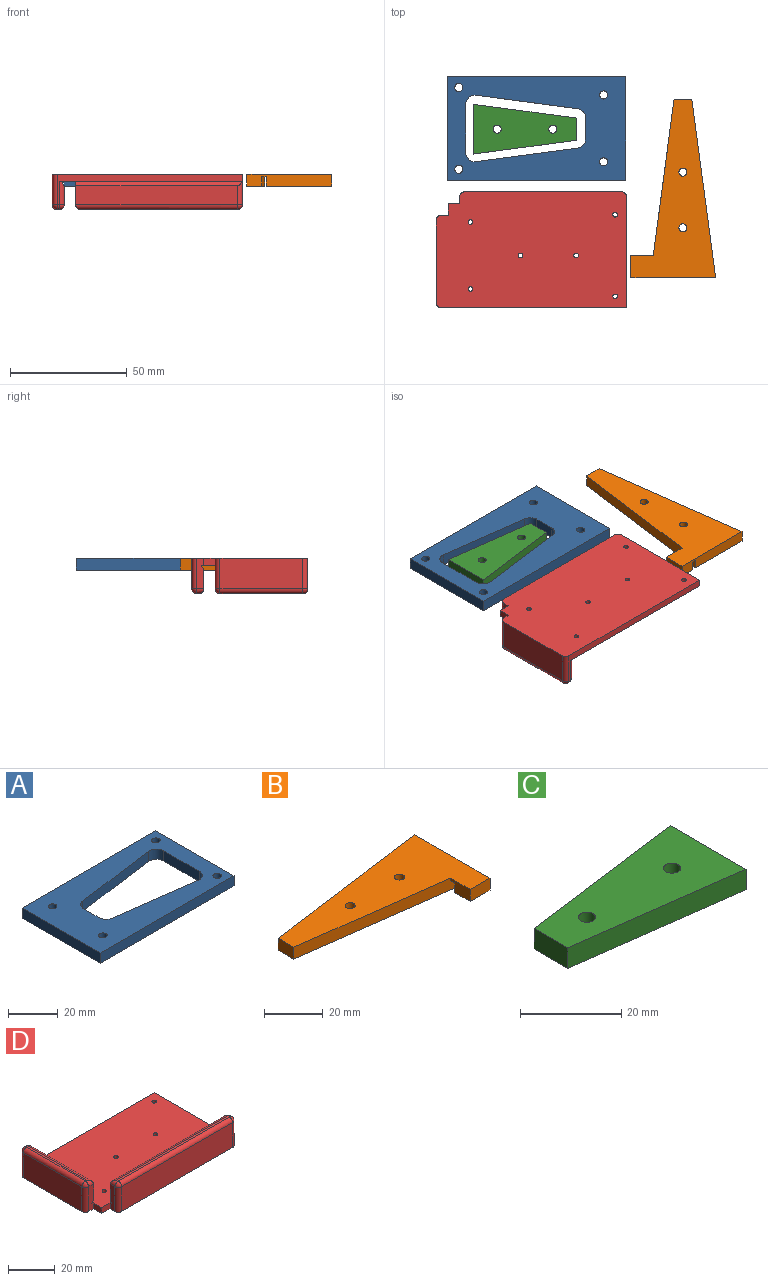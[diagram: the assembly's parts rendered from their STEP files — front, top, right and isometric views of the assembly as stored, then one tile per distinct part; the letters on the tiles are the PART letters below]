
ASSEMBLY  parts=4 mates=6
PART A: 22 faces, bbox 76.2x44.5x5 mm
  f0: plane 43.28x5.77mm, normal (0.13,0.99,0), area 218.3mm2, adj f8,f9,f18,f21
  f1: plane 8.89x5mm, normal (1,0,0), area 44.5mm2, adj f8,f9,f18,f19
  f2: plane 43.28x5.77mm, normal (0.13,-0.99,0), area 218.3mm2, adj f8,f9,f19,f20
  f3: plane 44.45x5mm, normal (-1,0,0), area 222.2mm2, adj f4,f6,f8,f9
  f4: plane 76.2x5mm, normal (0,-1,0), area 381mm2, adj f3,f5,f8,f9
  f5: plane 44.45x5mm, normal (1,0,0), area 222.2mm2, adj f4,f6,f8,f9
  f6: plane 76.2x5mm, normal (0,1,0), area 381mm2, adj f3,f5,f8,f9
  f7: plane 20.43x5mm, normal (-1,0,0), area 102.2mm2, adj f8,f9,f20,f21
  f8: plane 76.2x44.45mm, normal (0,0,-1), area 2075.8mm2, adj f0,f1,f2,f3,f4,f5,f6,f7
  f9: plane 76.2x44.45mm, normal (0,0,1), area 2198.3mm2, adj f0,f1,f2,f3,f4,f5,f6,f7
  f10: cylinder r=1.73mm len=3.45mm, axis (0,0,-1), area 31.3mm2, adj f9,f11
  f11: cone r=1.73mm half-angle=41deg, axis (0,0,-1), area 46.7mm2, adj f8,f10
  f12: cylinder r=1.73mm len=3.45mm, axis (0,0,-1), area 31.3mm2, adj f9,f13
  f13: cone r=1.73mm half-angle=41deg, axis (0,0,-1), area 46.7mm2, adj f8,f12
  f14: cylinder r=1.73mm len=3.45mm, axis (0,0,-1), area 31.3mm2, adj f9,f15
  f15: cone r=1.73mm half-angle=41deg, axis (0,0,-1), area 46.7mm2, adj f8,f14
  f16: cylinder r=1.73mm len=3.45mm, axis (0,0,-1), area 31.3mm2, adj f9,f17
  f17: cone r=1.73mm half-angle=41deg, axis (0,0,-1), area 46.7mm2, adj f8,f16
  f18: cylinder r=4mm len=5mm, axis (0,0,1), area 28.8mm2, adj f0,f1,f8,f9
  f19: cylinder r=4mm len=5mm, axis (0,0,-1), area 28.8mm2, adj f1,f2,f8,f9
  f20: cylinder r=4mm len=5mm, axis (0,0,1), area 34.1mm2, adj f2,f7,f8,f9
  f21: cylinder r=4mm len=5mm, axis (0,0,-1), area 34.1mm2, adj f0,f7,f8,f9
PART B: 15 faces, bbox 76.2x36.2x5 mm
  f0: plane 9.53x5mm, normal (-1,0,0), area 39.6mm2, adj f3,f4,f7,f8,f9,f10
  f1: plane 76.2x27.94mm, normal (0,0,-1), area 1274.8mm2, adj f2,f3,f5,f6,f12,f14
  f2: plane 7.62x5mm, normal (-1,0,0), area 38.1mm2, adj f1,f3,f6,f8
  f3: plane 76.2x10.16mm, normal (-0.13,-0.99,0), area 374.8mm2, adj f0,f1,f2,f5,f8,f10
  f4: plane 9.53x5mm, normal (0,-1,0), area 47.6mm2, adj f0,f5,f7,f8
  f5: plane 36.2x5mm, normal (1,0,0), area 172.9mm2, adj f1,f3,f4,f6,f7,f8,f9,f10
  f6: plane 76.2x10.16mm, normal (-0.13,0.99,0), area 384.4mm2, adj f1,f2,f5,f8
  f7: plane 9.53x7.51mm, normal (0,0,-1), area 65.5mm2, adj f0,f4,f5,f9
  f8: plane 76.2x36.2mm, normal (0,0,1), area 1420.8mm2, adj f0,f2,f3,f4,f5,f6,f11,f13
  f9: plane 9.53x4mm, normal (0.13,0.99,0), area 38.4mm2, adj f0,f5,f7,f10
  f10: plane 9.53x3.29mm, normal (0,0,-1), area 19.2mm2, adj f0,f3,f5,f9
  f11: cylinder r=1.73mm len=3.45mm, axis (0,0,-1), area 31.3mm2, adj f8,f12
  f12: cone r=1.73mm half-angle=41deg, axis (0,0,-1), area 46.7mm2, adj f1,f11
  f13: cylinder r=1.73mm len=3.45mm, axis (0,0,-1), area 31.3mm2, adj f8,f14
  f14: cone r=1.73mm half-angle=41deg, axis (0,0,-1), area 46.7mm2, adj f1,f13
PART C: 10 faces, bbox 44x21.2x5 mm
  f0: plane 21.23x5mm, normal (1,0,0), area 106.2mm2, adj f1,f3,f4,f5
  f1: plane 43.98x5.86mm, normal (-0.13,0.99,0), area 221.8mm2, adj f0,f2,f4,f5
  f2: plane 9.5x5mm, normal (-1,0,0), area 47.5mm2, adj f1,f3,f4,f5
  f3: plane 43.98x5.86mm, normal (-0.13,-0.99,0), area 221.8mm2, adj f0,f2,f4,f5
  f4: plane 43.98x21.23mm, normal (0,0,-1), area 595.8mm2, adj f0,f1,f2,f3,f7,f9
  f5: plane 43.98x21.23mm, normal (0,0,1), area 657.1mm2, adj f0,f1,f2,f3,f6,f8
  f6: cylinder r=1.73mm len=3.45mm, axis (0,0,-1), area 31.3mm2, adj f5,f7
  f7: cone r=1.73mm half-angle=41deg, axis (0,0,-1), area 46.7mm2, adj f4,f6
  f8: cylinder r=1.73mm len=3.45mm, axis (0,0,-1), area 31.3mm2, adj f5,f9
  f9: cone r=1.73mm half-angle=41deg, axis (0,0,-1), area 46.7mm2, adj f4,f8
PART D: 42 faces, bbox 81.2x49.5x15 mm
  f0: plane 37.45x8.16mm, normal (1,0,0), area 305.6mm2, adj f7,f15,f26,f31
  f1: plane 79.2x13mm, normal (0,1,0), area 247.6mm2, adj f4,f5,f6,f26,f27,f28
  f2: plane 5x3mm, normal (0,-1,0), area 15mm2, adj f3,f5,f6,f11
  f3: plane 5x3mm, normal (-1,0,0), area 15mm2, adj f2,f5,f6,f7
  f4: plane 47.45x13mm, normal (1,0,0), area 152.4mm2, adj f1,f5,f6,f16,f18,f19
  f5: plane 78.2x46.45mm, normal (0,0,1), area 3479.1mm2, adj f1,f2,f3,f4,f7,f11,f14,f15
  f6: plane 81.2x49.45mm, normal (0,0,-1), area 3918.1mm2, adj f1,f2,f3,f4,f7,f8,f11,f12
  f7: plane 13x3mm, normal (0,-1,0), area 38.1mm2, adj f0,f3,f5,f6,f15,f33,f35
  f8: plane 35.45x13mm, normal (-1,0,0), area 460.9mm2, adj f6,f27,f32,f35
  f9: plane 35.45x1mm, normal (0,0,1), area 35.5mm2, adj f28,f31,f32,f33
  f10: plane 69.2x8.16mm, normal (0,1,0), area 564.7mm2, adj f11,f14,f16,f20
  f11: plane 13x3mm, normal (-1,0,0), area 38.1mm2, adj f2,f5,f6,f10,f14,f22,f25
  f12: plane 67.2x13mm, normal (0,-1,0), area 873.6mm2, adj f6,f19,f23,f25
  f13: plane 67.2x1mm, normal (0,0,1), area 67.2mm2, adj f18,f20,f22,f23
  f14: plane 70.93x1.84mm, normal (0,0.88,-0.48), area 147.5mm2, adj f5,f10,f11,f16
  f15: plane 39.18x1.84mm, normal (0.88,0,-0.48), area 81mm2, adj f0,f5,f7,f26
  f16: cylinder r=2mm len=10mm, axis (0,0,-1), area 28.9mm2, adj f4,f5,f10,f14,f17
  f17: sphere r=2mm, area 6.3mm2, adj f16,f18,f20
  f18: cylinder r=2mm len=2mm, axis (0,1,0), area 3.1mm2, adj f4,f13,f17,f21
  f19: cylinder r=2mm len=13mm, axis (0,0,1), area 40.8mm2, adj f4,f6,f12,f21
  f20: cylinder r=2mm len=69.2mm, axis (1,0,0), area 215.1mm2, adj f10,f13,f17,f22
  f21: sphere r=2mm, area 6.3mm2, adj f18,f19,f23
  f22: cylinder r=2mm len=3mm, axis (0,1,0), area 7.1mm2, adj f11,f13,f20,f24
  f23: cylinder r=2mm len=67.2mm, axis (-1,0,0), area 211.1mm2, adj f12,f13,f21,f24
  f24: sphere r=2mm, area 6.3mm2, adj f22,f23,f25
  f25: cylinder r=2mm len=13mm, axis (0,0,-1), area 40.8mm2, adj f6,f11,f12,f24
  f26: cylinder r=2mm len=10mm, axis (0,0,1), area 28.9mm2, adj f0,f1,f5,f15,f29
  f27: cylinder r=2mm len=13mm, axis (0,0,1), area 40.8mm2, adj f1,f6,f8,f30
  f28: cylinder r=2mm len=2mm, axis (-1,0,0), area 3.1mm2, adj f1,f9,f29,f30
  f29: sphere r=2mm, area 6.3mm2, adj f26,f28,f31
  f30: sphere r=2mm, area 6.3mm2, adj f27,f28,f32
  f31: cylinder r=2mm len=37.45mm, axis (0,-1,0), area 115.4mm2, adj f0,f9,f29,f33
  f32: cylinder r=2mm len=35.45mm, axis (0,1,0), area 111.4mm2, adj f8,f9,f30,f34
  f33: cylinder r=2mm len=3mm, axis (-1,0,0), area 7.1mm2, adj f7,f9,f31,f34
  f34: sphere r=2mm, area 6.3mm2, adj f32,f33,f35
  f35: cylinder r=2mm len=13mm, axis (0,0,1), area 40.8mm2, adj f6,f7,f8,f34
  f36: cylinder r=1mm len=3mm, axis (0,0,-1), area 18.8mm2, adj f5,f6
  f37: cylinder r=1mm len=3mm, axis (0,0,-1), area 18.8mm2, adj f5,f6
  f38: cylinder r=1mm len=3mm, axis (0,0,-1), area 18.8mm2, adj f5,f6
  f39: cylinder r=1mm len=3mm, axis (0,0,-1), area 18.8mm2, adj f5,f6
  f40: cylinder r=1mm len=3mm, axis (0,0,-1), area 18.8mm2, adj f5,f6
  f41: cylinder r=1mm len=3mm, axis (0,0,-1), area 18.8mm2, adj f5,f6
PLACE A rot(axis=(0,0,-1),180deg) t=(-45.58,-17.87,27.29)mm
PLACE B rot(axis=(0,0,-1),90deg) t=(55,-81.8,27.29)mm
PLACE C rot(axis=(0,0,-1),180deg) t=(-45.88,-18.2,27.29)mm
PLACE D rot(axis=(1,0,0),180deg) t=(30.79,-72.2,27.29)mm
MATE parallel A.f6 <-> D.f1  axis (0,-1,0) through (-7.48,-40.09,24.79)mm
MATE planar A.f9 <-> B.f11  axis (0,0,1) through (-24.15,-17.87,27.29)mm
MATE parallel B.f5 <-> D.f1  axis (0,-1,0) through (51.38,-81.8,24.81)mm
MATE parallel C.f0 <-> D.f8  axis (-1,0,0) through (-34.53,-18.19,24.79)mm
MATE planar A.f9 <-> C.f6  axis (0,0,1) through (-24.15,-17.87,27.29)mm
MATE planar D.f39 <-> C.f6  axis (0,0,1) through (9.36,-72.21,27.29)mm
